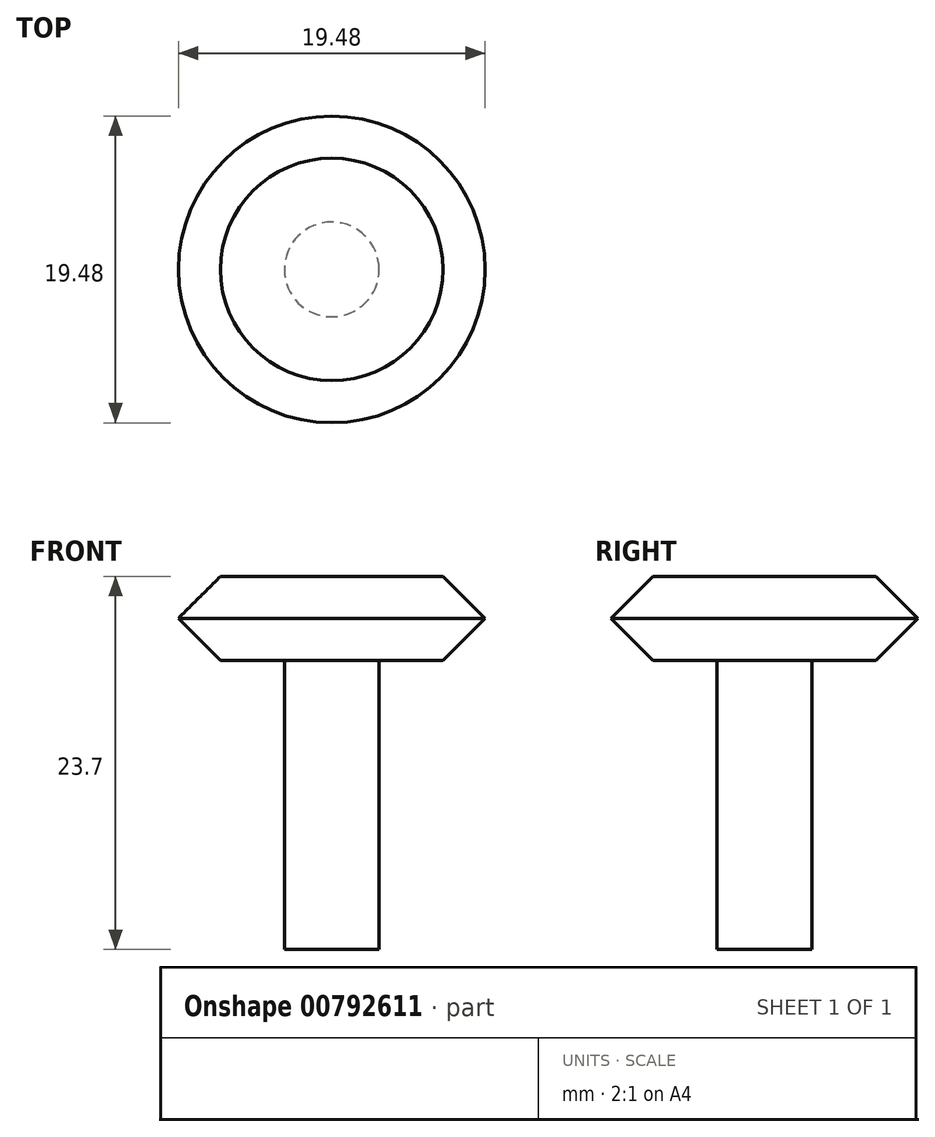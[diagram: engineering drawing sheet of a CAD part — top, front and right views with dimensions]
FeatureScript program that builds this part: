
annotation { "Feature Type Name" : "Feature", "Feature Type Description" : "" }
export const myFeature = defineFeature(function(context is Context, id is Id, definition is map)
    precondition{}
    {
        {
            var Q0;
            Q0=qCreatedBy(makeId("Front.planeOp"),FACE);
            var sketch = newSketch(context, id + "F0", { "sketchPlane" : qUnion([Q0])});
            skLineSegment(sketch, "E0", {"start": v(0, 0) * mm, "end": v(0, 23.7) * mm});
            skLineSegment(sketch, "E1", {"start": v(0, 23.7) * mm, "end": v(7.07, 23.7) * mm});
            skLineSegment(sketch, "E2", {"start": v(7.07, 23.7) * mm, "end": v(9.74, 21.03) * mm});
            skLineSegment(sketch, "E3", {"start": v(9.74, 21.03) * mm, "end": v(7.07, 18.36) * mm});
            skLineSegment(sketch, "E4", {"start": v(7.07, 18.36) * mm, "end": v(3, 18.36) * mm});
            skLineSegment(sketch, "E5", {"start": v(3, 18.36) * mm, "end": v(3, 0) * mm});
            skLineSegment(sketch, "E6", {"start": v(3, 0) * mm, "end": v(0, 0) * mm});
            skSolve(sketch);
        }
        {
            var Q0;
            Q0=makeQuery(id+"F0.imprint","IMPRINT",FACE,{"disambiguationData":[TD([[makeQuery(id+"F0.imprint","IMPRINT",EDGE,{"derivedFrom":sQuery(id+"F0.wireOp",EDGE,"E0")}),-1.0]])]});
            var Q1;
            Q1=sQuery(id+"F0.wireOp",EDGE,"E0");
            revolve(context, id + "F1", {"surfaceOperationType" : NewSurfaceOperationType.NEW, "entities" : qUnion([Q0]), "axis" : qUnion([Q1]), "revolveType" : RevolveType.FULL});
        }
    });
